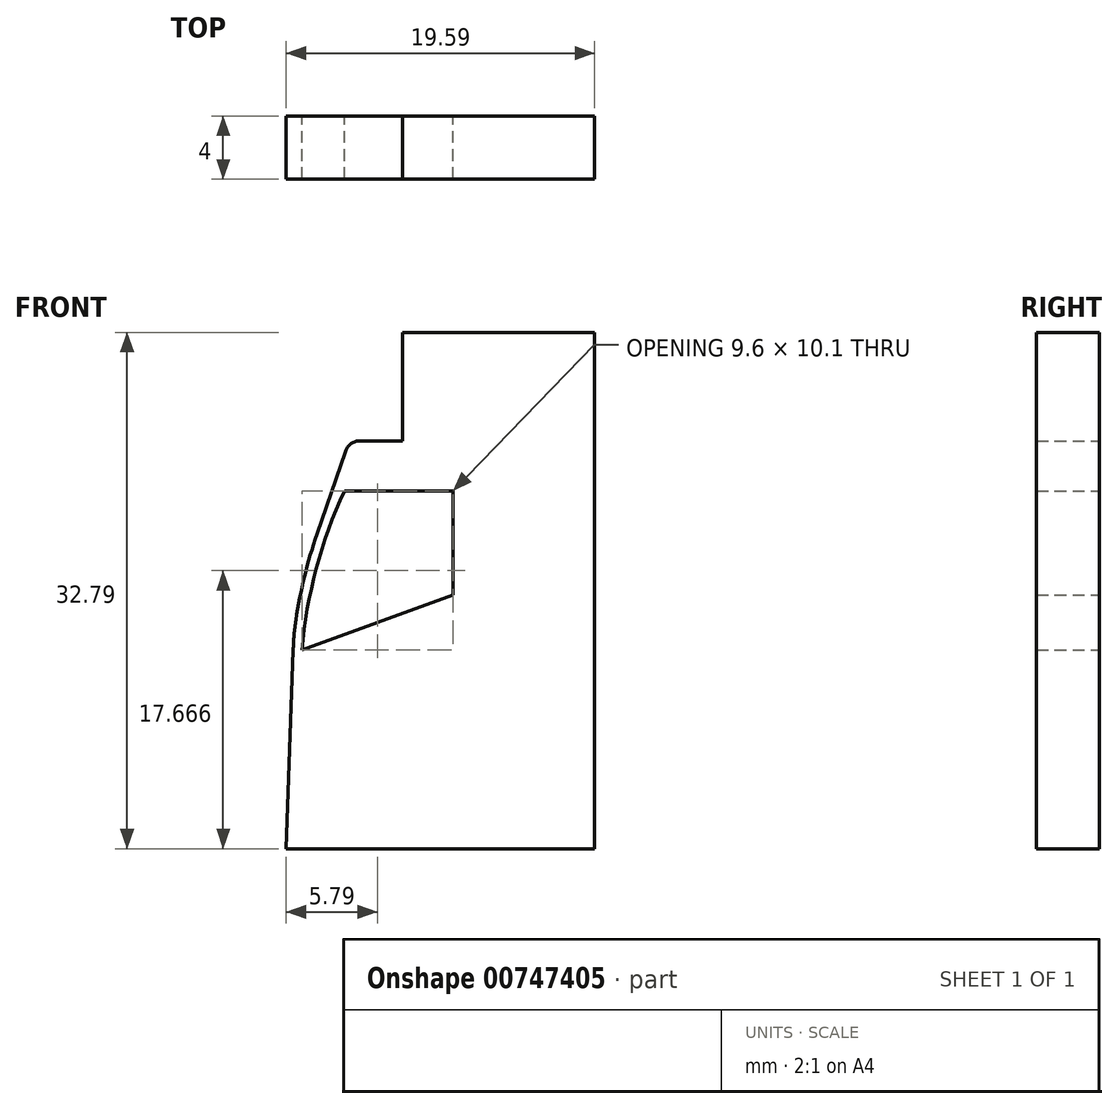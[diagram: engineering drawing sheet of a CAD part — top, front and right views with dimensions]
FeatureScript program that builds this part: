
annotation { "Feature Type Name" : "Feature", "Feature Type Description" : "" }
export const myFeature = defineFeature(function(context is Context, id is Id, definition is map)
    precondition{}
    {
        {
            var Q0;
            Q0=qCreatedBy(makeId("Front.planeOp"),FACE);
            var sketch = newSketch(context, id + "F0", { "sketchPlane" : qUnion([Q0])});
            skArc(sketch, "E0.0", {"start": v(-82.14, 38.15) * mm, "mid": v(-81.6, 40.9) * mm, "end": v(-80.8, 43.6) * mm});
            skLineSegment(sketch, "E1", {"start": v(-80.8, 43.6) * mm, "end": v(-78.76, 49.53) * mm});
            skLineSegment(sketch, "E2", {"start": v(-82.31, 36.23) * mm, "end": v(-82.75, 23.61) * mm});
            skPoint(sketch, "E3.visualSharp", {"position": v(-82.29, 37) * mm});
            skArc(sketch, "E3.filletArc", {"start": v(-82.14, 38.15) * mm, "mid": v(-82.25, 37.2) * mm, "end": v(-82.31, 36.23) * mm});
            skLineSegment(sketch, "E4", {"start": v(-75.36, 49.53) * mm, "end": v(-78.76, 49.53) * mm});
            skLineSegment(sketch, "E5", {"start": v(-75.36, 49.53) * mm, "end": v(-75.36, 56.4) * mm});
            skLineSegment(sketch, "E6", {"start": v(-75.36, 56.4) * mm, "end": v(-63.16, 56.4) * mm});
            skLineSegment(sketch, "E7", {"start": v(-63.16, 56.4) * mm, "end": v(-63.16, 23.61) * mm});
            skLineSegment(sketch, "E8", {"start": v(-63.16, 23.61) * mm, "end": v(-82.75, 23.61) * mm});
            skArc(sketch, "E9.0", {"start": v(-81.76, 36.23) * mm, "mid": v(-80.85, 41.4) * mm, "end": v(-79.05, 46.33) * mm});
            skLineSegment(sketch, "E9.1", {"start": v(-79.05, 46.33) * mm, "end": v(-72.16, 46.33) * mm});
            skLineSegment(sketch, "E9.2", {"start": v(-72.16, 39.72) * mm, "end": v(-81.76, 36.23) * mm});
            skLineSegment(sketch, "E9.3", {"start": v(-72.16, 46.33) * mm, "end": v(-72.16, 39.72) * mm});
            skSolve(sketch);
        }
        {
            var Q0;
            Q0=makeQuery(id+"F0.imprint","IMPRINT",FACE,{"disambiguationData":[TD([[makeQuery(id+"F0.imprint","IMPRINT",EDGE,{"derivedFrom":sQuery(id+"F0.wireOp",EDGE,"E0.0")}),-1.0]])]});
            var Q1;
            Q1=makeQuery(id+"F0.imprint","IMPRINT",FACE,{"disambiguationData":[TD([[makeQuery(id+"F0.imprint","IMPRINT",EDGE,{"derivedFrom":sQuery(id+"F0.wireOp",EDGE,"E9.0")}),-1.0]])]});
            extrude(context, id + "F1", {"entities" : qUnion([Q0, Q1]), "depth" : 4 * mm, "offsetDistance" : 25 * mm});
        }
        {
            var Q0;
            Q0=makeQuery(id+"F1.opExtrude","SWEPT_EDGE",EDGE,{"disambiguationData":[OSD([sQuery(id+"F0.wireOp",EDGE,"E1"),sQuery(id+"F0.wireOp",EDGE,"E4")])]});
            fillet(context, id + "F2", {"entities" : qUnion([Q0]), "radius" : 1 * mm, "tangentPropagation" : true, "allowEdgeOverflow" : false});
        }
    });
